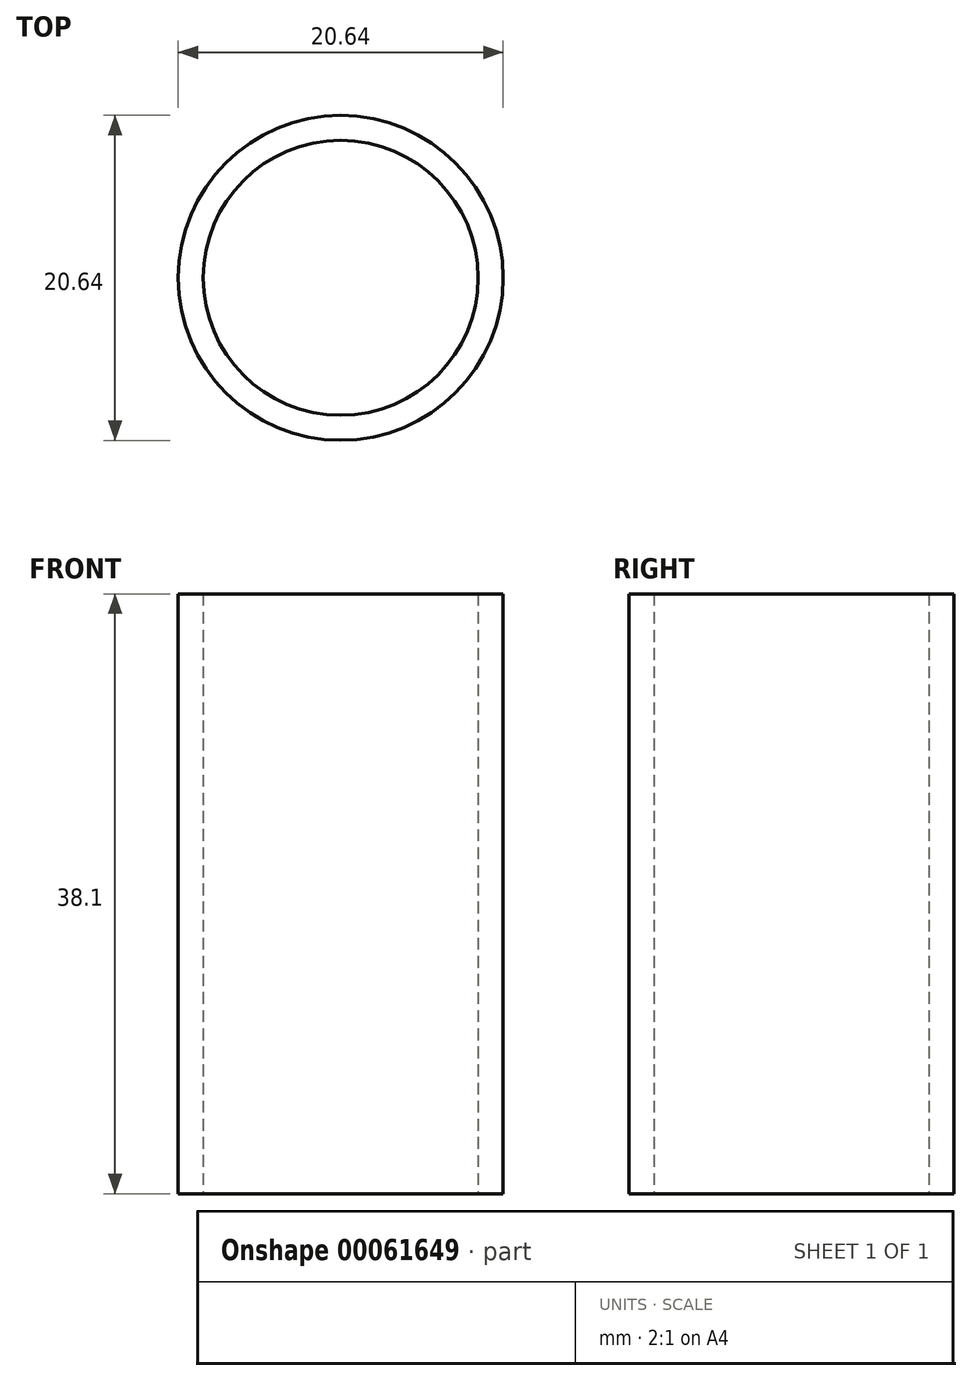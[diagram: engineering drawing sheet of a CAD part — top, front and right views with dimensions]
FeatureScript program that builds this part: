
annotation { "Feature Type Name" : "Feature", "Feature Type Description" : "" }
export const myFeature = defineFeature(function(context is Context, id is Id, definition is map)
    precondition{}
    {
        {
            var Q0;
            Q0=qCreatedBy(makeId("Top.planeOp"),FACE);
            var sketch = newSketch(context, id + "F0", { "sketchPlane" : qUnion([Q0])});
            skCircle(sketch, "E0", {"center": v(0, 0) * mm, "radius": 10.32 * mm});
            skSolve(sketch);
        }
        {
            var Q0;
            Q0=qCreatedBy(makeId("Top.planeOp"),FACE);
            var sketch = newSketch(context, id + "F1", { "sketchPlane" : qUnion([Q0])});
            skCircle(sketch, "E1", {"center": v(0, 0) * mm, "radius": 8.73 * mm});
            skSolve(sketch);
        }
        {
            var Q0;
            Q0 = qSketchRegion(id + "F0", true);
            extrude(context, id + "F2", {"entities" : qUnion([Q0]), "depth" : 38.1 * mm});
        }
        {
            var Q0;
            Q0 = qSketchRegion(id + "F1", true);
            extrude(context, id + "F3", {"entities" : qUnion([Q0]), "operationType" : NewBodyOperationType.REMOVE, "depth" : 38.1 * mm});
        }
    });
